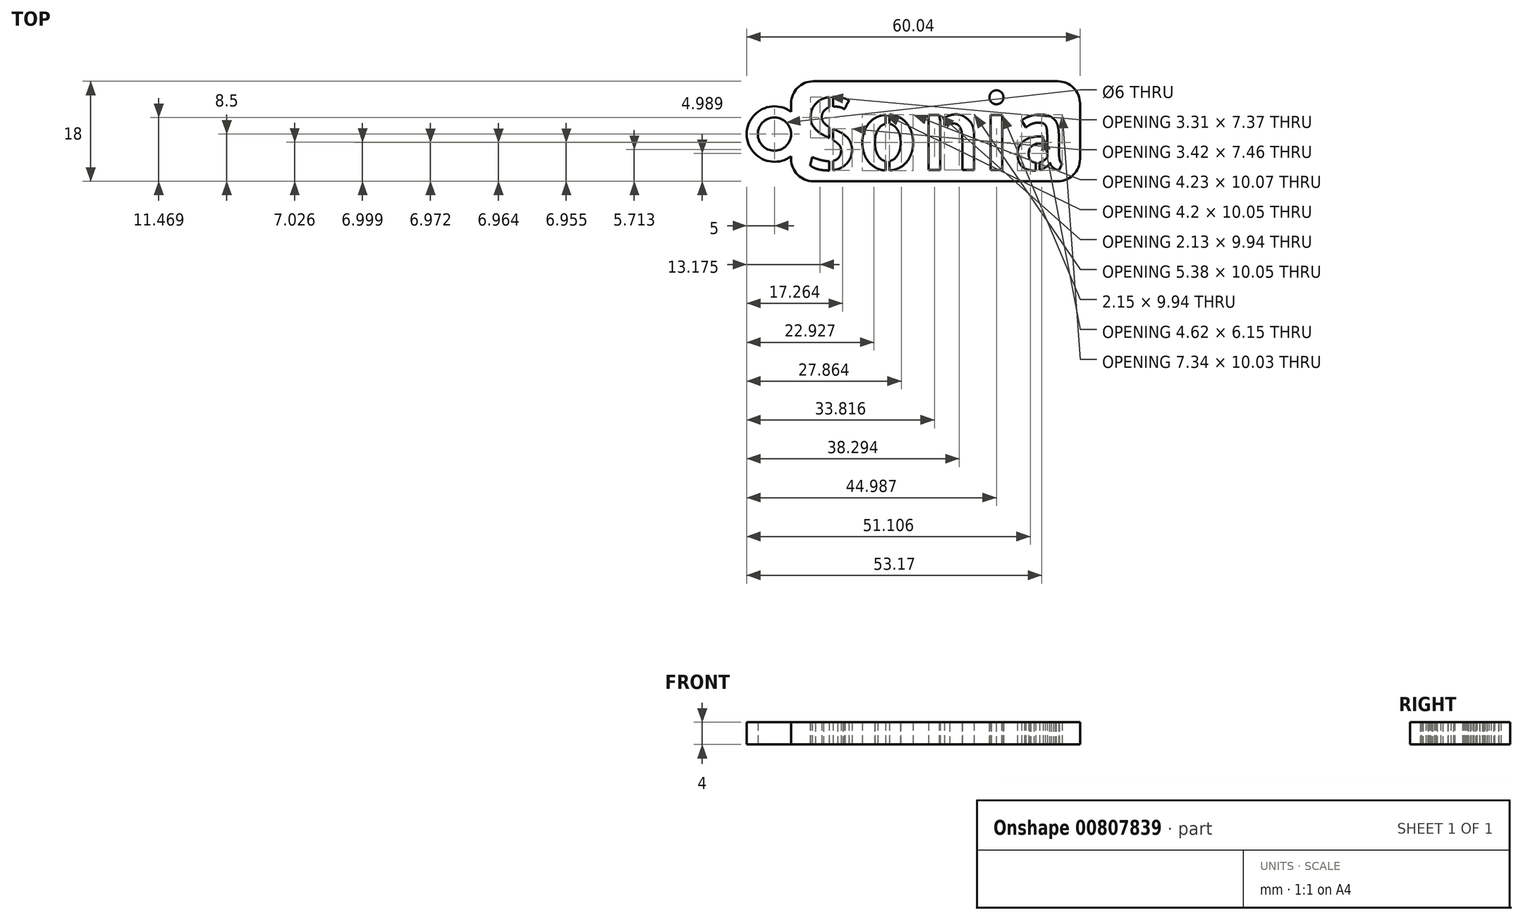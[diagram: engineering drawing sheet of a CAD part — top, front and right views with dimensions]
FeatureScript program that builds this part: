
annotation { "Feature Type Name" : "Feature", "Feature Type Description" : "" }
export const myFeature = defineFeature(function(context is Context, id is Id, definition is map)
    precondition{}
    {
        {
            var Q0;
            Q0=qCreatedBy(makeId("Top.planeOp"),FACE);
            var sketch = newSketch(context, id + "F0", { "sketchPlane" : qUnion([Q0])});
            skLineSegment(sketch, "E0.bottom", {"start": v(-2, -2) * mm, "end": v(50.04, -2) * mm});
            skLineSegment(sketch, "E0.top", {"start": v(-2, 16) * mm, "end": v(50.04, 16) * mm});
            skLineSegment(sketch, "E0.left", {"start": v(-2, -2) * mm, "end": v(-2, 2.5) * mm});
            skLineSegment(sketch, "E0.right", {"start": v(50.04, -2) * mm, "end": v(50.04, 16) * mm});
            skArc(sketch, "E1", {"start": v(-2, 10.5) * mm, "mid": v(-10, 6.5) * mm, "end": v(-2, 2.5) * mm});
            skLineSegment(sketch, "E2.trimOffspring", {"start": v(-2, 10.5) * mm, "end": v(-2, 16) * mm});
            skCircle(sketch, "E3", {"center": v(-5, 6.5) * mm, "radius": 3 * mm});
            skText(sketch, "E4", { "text": "Sonia", "fontName": "AllertaStencil-Regular.ttf"});
            skLineSegment(sketch, "E5", {"start": v(50.04, 7) * mm, "end": v(0, 6.5) * mm, "construction": true});
            skLineSegment(sketch, "E6", {"start": v(0, 6.5) * mm, "end": v(-10.53, 6.5) * mm, "construction": true});
            const initialGuessF0  = {"E4": [0, 0, 1, 0, 0.013]};
            skSetInitialGuess(sketch, initialGuessF0);
            skSolve(sketch);
        }
        {
            var Q0;
            Q0=makeQuery(id+"F0.imprint","IMPRINT",FACE,{"disambiguationData":[TD([[makeQuery(id+"F0.imprint","IMPRINT",EDGE,{"derivedFrom":sQuery(id+"F0.wireOp",EDGE,"E0.bottom")}),1.0]])]});
            extrude(context, id + "F1", {"entities" : qUnion([Q0]), "depth" : 4 * mm, "offsetDistance" : 25 * mm});
        }
        {
            var Q0;
            Q0=makeQuery(id+"F1.opExtrude","SWEPT_EDGE",EDGE,{"disambiguationData":[OSD([sQuery(id+"F0.wireOp",EDGE,"E0.bottom"),sQuery(id+"F0.wireOp",EDGE,"E0.right")])]});
            var Q1;
            Q1=makeQuery(id+"F1.opExtrude","SWEPT_EDGE",EDGE,{"disambiguationData":[OSD([sQuery(id+"F0.wireOp",EDGE,"E0.top"),sQuery(id+"F0.wireOp",EDGE,"E0.right")])]});
            var Q2;
            Q2=makeQuery(id+"F1.opExtrude","SWEPT_EDGE",EDGE,{"disambiguationData":[OSD([sQuery(id+"F0.wireOp",EDGE,"E0.bottom"),sQuery(id+"F0.wireOp",EDGE,"E0.left")])]});
            var Q3;
            Q3=makeQuery(id+"F1.opExtrude","SWEPT_EDGE",EDGE,{"disambiguationData":[OSD([sQuery(id+"F0.wireOp",EDGE,"E0.top"),sQuery(id+"F0.wireOp",EDGE,"E2.trimOffspring")])]});
            fillet(context, id + "F2", {"entities" : qUnion([Q0, Q1, Q2, Q3]), "radius" : 4 * mm, "tangentPropagation" : true, "allowEdgeOverflow" : false});
        }
    });
